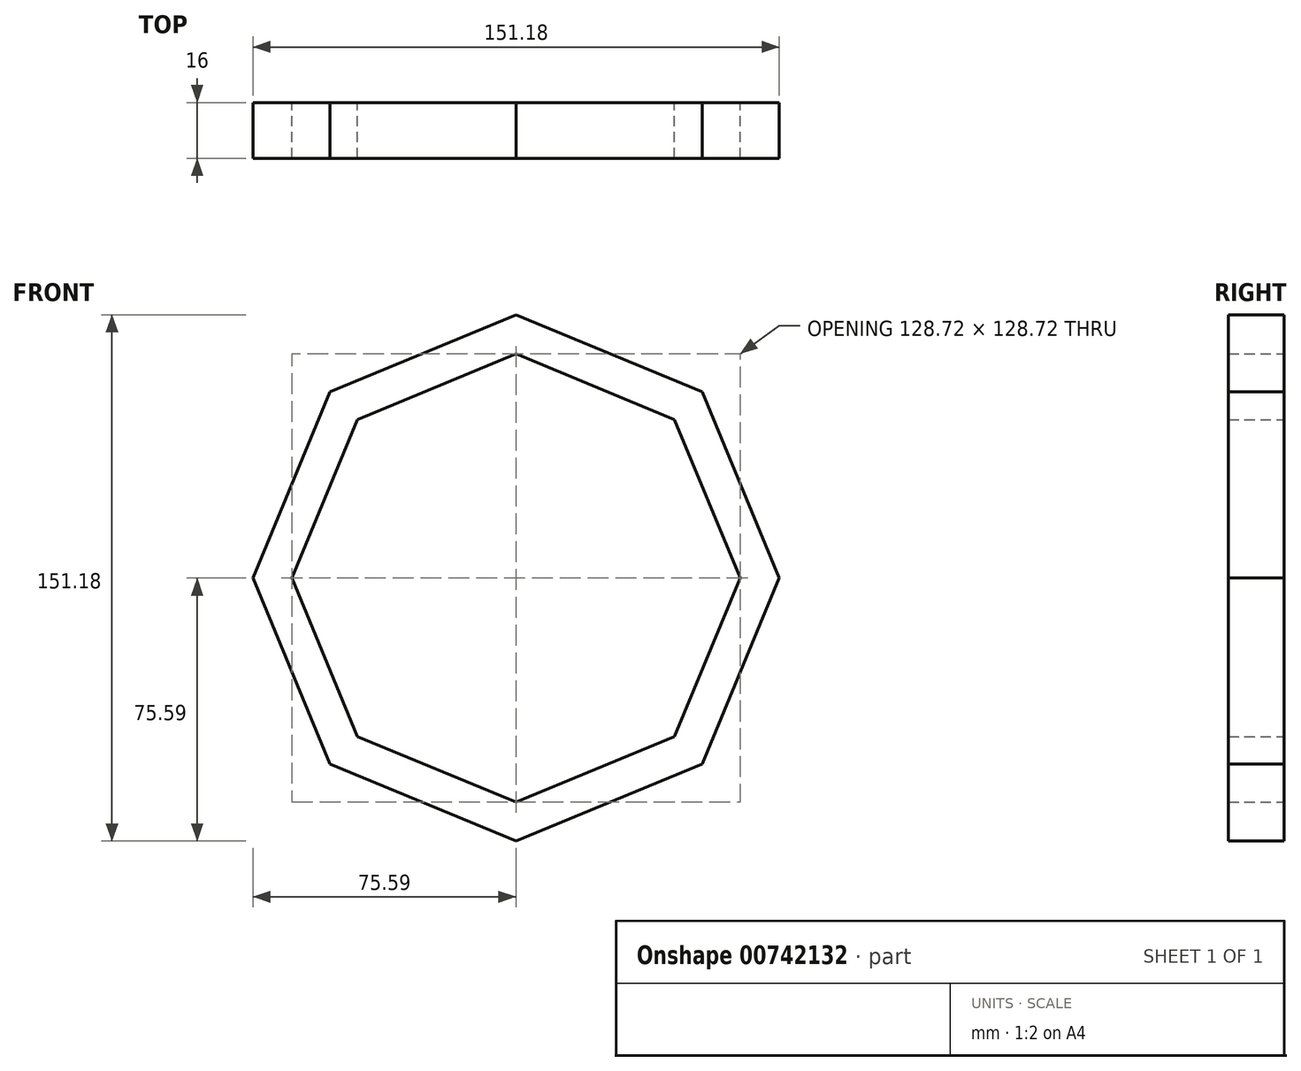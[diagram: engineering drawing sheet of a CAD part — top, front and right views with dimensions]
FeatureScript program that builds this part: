
annotation { "Feature Type Name" : "Feature", "Feature Type Description" : "" }
export const myFeature = defineFeature(function(context is Context, id is Id, definition is map)
    precondition{}
    {
        {
            var Q0;
            Q0=qCreatedBy(makeId("Front.planeOp"),FACE);
            var sketch = newSketch(context, id + "F0", { "sketchPlane" : qUnion([Q0])});
            skCircle(sketch, "E0.cCircle", {"center": v(0, 0) * mm, "radius": 75.59 * mm, "construction": true});
            skLineSegment(sketch, "E0.0", {"start": v(0, 75.59) * mm, "end": v(53.45, 53.45) * mm});
            skLineSegment(sketch, "E0.1", {"start": v(53.45, 53.45) * mm, "end": v(75.59, 0) * mm});
            skLineSegment(sketch, "E0.2", {"start": v(75.59, 0) * mm, "end": v(53.45, -53.45) * mm});
            skLineSegment(sketch, "E0.3", {"start": v(53.45, -53.45) * mm, "end": v(0, -75.59) * mm});
            skLineSegment(sketch, "E0.4", {"start": v(0, -75.59) * mm, "end": v(-53.45, -53.45) * mm});
            skLineSegment(sketch, "E0.5", {"start": v(-53.45, -53.45) * mm, "end": v(-75.59, 0) * mm});
            skLineSegment(sketch, "E0.6", {"start": v(-75.59, 0) * mm, "end": v(-53.45, 53.45) * mm});
            skLineSegment(sketch, "E0.7", {"start": v(-53.45, 53.45) * mm, "end": v(0, 75.59) * mm});
            skCircle(sketch, "E1.cCircle", {"center": v(0, 0) * mm, "radius": 64.36 * mm, "construction": true});
            skLineSegment(sketch, "E1.0", {"start": v(0, 64.36) * mm, "end": v(45.5, 45.5) * mm});
            skLineSegment(sketch, "E1.1", {"start": v(45.5, 45.5) * mm, "end": v(64.36, 0) * mm});
            skLineSegment(sketch, "E1.2", {"start": v(64.36, 0) * mm, "end": v(45.5, -45.5) * mm});
            skLineSegment(sketch, "E1.3", {"start": v(45.5, -45.5) * mm, "end": v(0, -64.36) * mm});
            skLineSegment(sketch, "E1.4", {"start": v(0, -64.36) * mm, "end": v(-45.5, -45.5) * mm});
            skLineSegment(sketch, "E1.5", {"start": v(-45.5, -45.5) * mm, "end": v(-64.36, 0) * mm});
            skLineSegment(sketch, "E1.6", {"start": v(-64.36, 0) * mm, "end": v(-45.5, 45.5) * mm});
            skLineSegment(sketch, "E1.7", {"start": v(-45.5, 45.5) * mm, "end": v(0, 64.36) * mm});
            skSolve(sketch);
        }
        {
            var Q0;
            Q0 = qSketchRegion(id + "F0", true);
            extrude(context, id + "F1", {"entities" : qUnion([Q0]), "depth" : 16 * mm, "offsetDistance" : 25.4 * mm});
        }
    });
